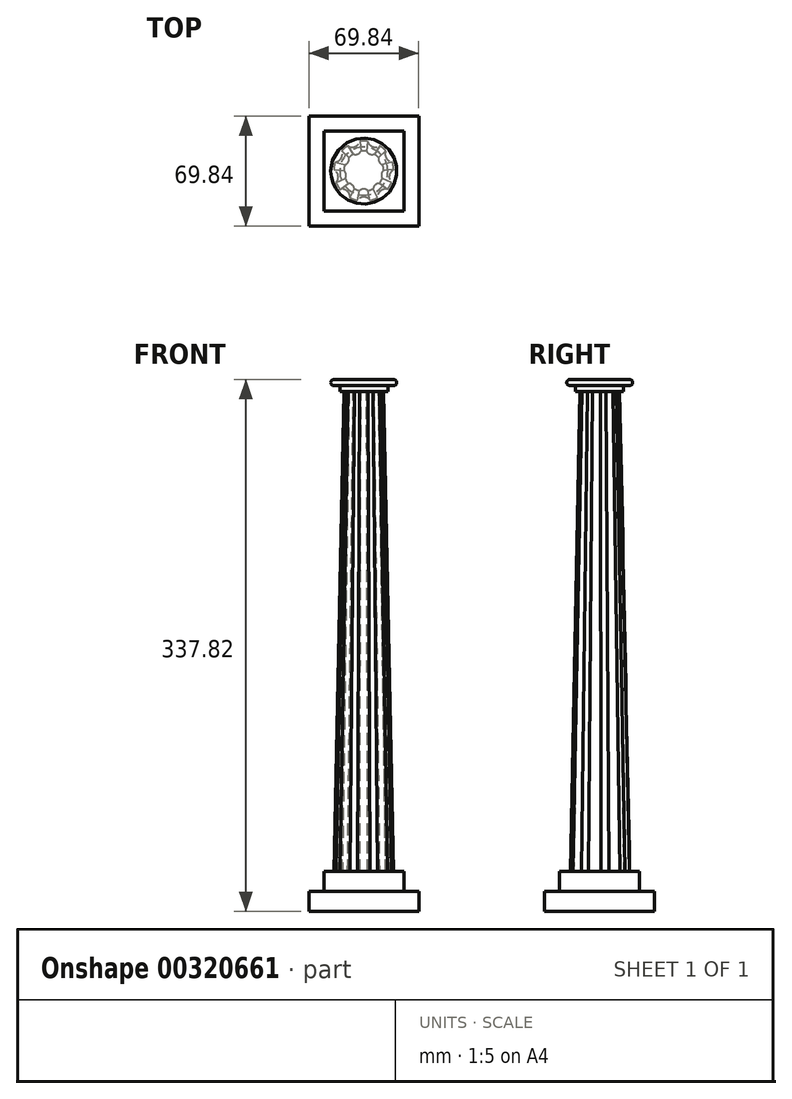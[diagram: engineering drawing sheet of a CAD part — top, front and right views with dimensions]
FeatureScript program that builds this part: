
annotation { "Feature Type Name" : "Feature", "Feature Type Description" : "" }
export const myFeature = defineFeature(function(context is Context, id is Id, definition is map)
    precondition{}
    {
        {
            var Q0;
            Q0=qCreatedBy(makeId("Top.planeOp"),FACE);
            var sketch = newSketch(context, id + "F0", { "sketchPlane" : qUnion([Q0])});
            skCircle(sketch, "E0", {"center": v(0, 0) * mm, "radius": 19.05 * mm});
            skArc(sketch, "E1", {"start": v(4.1, -18.6) * mm, "mid": v(0, -16.51) * mm, "end": v(-4.1, -18.6) * mm});
            skArc(sketch, "E2.1.0", {"start": v(15.1, -11.6) * mm, "mid": v(10.61, -12.65) * mm, "end": v(8.8, -16.9) * mm});
            skArc(sketch, "E2.2.0", {"start": v(19.03, 0.82) * mm, "mid": v(16.26, -2.87) * mm, "end": v(17.6, -7.28) * mm});
            skArc(sketch, "E2.3.0", {"start": v(14.06, 12.86) * mm, "mid": v(14.3, 8.25) * mm, "end": v(18.16, 5.74) * mm});
            skArc(sketch, "E2.4.0", {"start": v(2.5, 18.89) * mm, "mid": v(5.65, 15.51) * mm, "end": v(10.22, 16.07) * mm});
            skArc(sketch, "E2.5.0", {"start": v(-10.22, 16.07) * mm, "mid": v(-5.65, 15.51) * mm, "end": v(-2.5, 18.89) * mm});
            skArc(sketch, "E2.6.0", {"start": v(-18.16, 5.74) * mm, "mid": v(-14.3, 8.26) * mm, "end": v(-14.06, 12.86) * mm});
            skArc(sketch, "E2.7.0", {"start": v(-17.6, -7.28) * mm, "mid": v(-16.26, -2.87) * mm, "end": v(-19.03, 0.82) * mm});
            skArc(sketch, "E2.8.0", {"start": v(-8.8, -16.9) * mm, "mid": v(-10.61, -12.65) * mm, "end": v(-15.1, -11.6) * mm});
            skSolve(sketch);
        }
        {
            var Q0;
            Q0=qCreatedBy(makeId("Top.planeOp"),FACE);
            cPlane(context, id + "F1", {"entities" : qUnion([Q0]), "cplaneType" : CPlaneType.OFFSET, "offset" : 304.8 * mm, "width" : 152.4 * mm, "height" : 152.4 * mm});
        }
        {
            var Q0;
            Q0=qCreatedBy(id+"F1.planeOp",FACE);
            var sketch = newSketch(context, id + "F2", { "sketchPlane" : qUnion([Q0])});
            skCircle(sketch, "E3", {"center": v(0, 0) * mm, "radius": 12.7 * mm});
            skArc(sketch, "E4", {"start": v(2.58, -12.44) * mm, "mid": v(0, -11.43) * mm, "end": v(-2.58, -12.44) * mm});
            skArc(sketch, "E5.1.0", {"start": v(9.97, -7.87) * mm, "mid": v(7.35, -8.76) * mm, "end": v(6.02, -11.18) * mm});
            skArc(sketch, "E5.2.0", {"start": v(12.7, 0.38) * mm, "mid": v(11.26, -1.98) * mm, "end": v(11.8, -4.7) * mm});
            skArc(sketch, "E5.3.0", {"start": v(9.48, 8.45) * mm, "mid": v(9.9, 5.71) * mm, "end": v(12.06, 3.98) * mm});
            skArc(sketch, "E5.4.0", {"start": v(1.83, 12.57) * mm, "mid": v(3.9, 10.74) * mm, "end": v(6.68, 10.8) * mm});
            skArc(sketch, "E5.5.0", {"start": v(-6.68, 10.8) * mm, "mid": v(-3.9, 10.74) * mm, "end": v(-1.83, 12.57) * mm});
            skArc(sketch, "E5.6.0", {"start": v(-12.06, 3.98) * mm, "mid": v(-9.9, 5.72) * mm, "end": v(-9.48, 8.45) * mm});
            skArc(sketch, "E5.7.0", {"start": v(-11.8, -4.7) * mm, "mid": v(-11.26, -1.98) * mm, "end": v(-12.7, 0.38) * mm});
            skArc(sketch, "E5.8.0", {"start": v(-6.02, -11.18) * mm, "mid": v(-7.35, -8.76) * mm, "end": v(-9.97, -7.87) * mm});
            skSolve(sketch);
        }
        {
            var Q0;
            {var subQ0=sQuery(id+"F0.wireOp",EDGE,"E1");Q0=makeQuery(id+"F0.imprint","IMPRINT",FACE,{"disambiguationData":[TD([[makeQuery(id+"F0.imprint","IMPRINT",EDGE,{"derivedFrom":subQ0}),-1.0]])]});}
            var Q1;
            {var subQ0=sQuery(id+"F2.wireOp",EDGE,"E4");Q1=makeQuery(id+"F2.imprint","IMPRINT",FACE,{"disambiguationData":[TD([[makeQuery(id+"F2.imprint","IMPRINT",EDGE,{"derivedFrom":subQ0}),-1.0]])]});}
            loft(context, id + "F3", {"sheetProfilesArray" : [{ "sheetProfileEntities" : qUnion([Q0]) }, { "sheetProfileEntities" : qUnion([Q1]) }]});
        }
        {
            var Q0;
            Q0=qCreatedBy(makeId("Right.planeOp"),FACE);
            var sketch = newSketch(context, id + "F4", { "sketchPlane" : qUnion([Q0])});
            skLineSegment(sketch, "E6", {"start": v(0, 304.8) * mm, "end": v(0, 312.42) * mm});
            skLineSegment(sketch, "E7", {"start": v(0, 312.42) * mm, "end": v(19.05, 312.42) * mm});
            skLineSegment(sketch, "E8", {"start": v(0, 304.8) * mm, "end": v(15.24, 304.8) * mm});
            skLineSegment(sketch, "E9", {"start": v(15.24, 304.8) * mm, "end": v(15.24, 308.6) * mm});
            skLineSegment(sketch, "E10", {"start": v(15.24, 308.6) * mm, "end": v(19.05, 308.6) * mm});
            skLineSegment(sketch, "E11", {"start": v(19.05, 308.6) * mm, "end": v(19.05, 312.42) * mm});
            skCircle(sketch, "E12", {"center": v(19.05, 310.51) * mm, "radius": 1.9 * mm});
            skSolve(sketch);
        }
        {
            var Q0;
            Q0=makeQuery(id+"F4.imprint","IMPRINT",FACE,{"disambiguationData":[TD([[makeQuery(id+"F4.imprint","IMPRINT",EDGE,{"derivedFrom":sQuery(id+"F4.wireOp",EDGE,"E6")}),-1.0]])]});
            var Q1;
            {var subQ0=sQuery(id+"F4.wireOp",EDGE,"E11");Q1=makeQuery(id+"F4.imprint","IMPRINT",FACE,{"disambiguationData":[TD([[makeQuery(id+"F4.imprint","IMPRINT",EDGE,{"derivedFrom":subQ0}),1.0]])]});}
            var Q2;
            {var subQ0=sQuery(id+"F4.wireOp",EDGE,"E11");Q2=makeQuery(id+"F4.imprint","IMPRINT",FACE,{"disambiguationData":[TD([[makeQuery(id+"F4.imprint","IMPRINT",EDGE,{"derivedFrom":subQ0}),-1.0]])]});}
            var Q3;
            Q3=sQuery(id+"F4.wireOp",EDGE,"E6");
            revolve(context, id + "F5", {"operationType" : NewBodyOperationType.ADD, "entities" : qUnion([Q0, Q1, Q2]), "axis" : qUnion([Q3]), "revolveType" : RevolveType.FULL});
        }
        {
            var Q0;
            Q0=qCreatedBy(makeId("Top.planeOp"),FACE);
            var sketch = newSketch(context, id + "F6", { "sketchPlane" : qUnion([Q0])});
            skLineSegment(sketch, "E13.bottom", {"start": v(25.4, 25.4) * mm, "end": v(-25.4, 25.4) * mm});
            skLineSegment(sketch, "E13.top", {"start": v(25.4, -25.4) * mm, "end": v(-25.4, -25.4) * mm});
            skLineSegment(sketch, "E13.left", {"start": v(25.4, 25.4) * mm, "end": v(25.4, -25.4) * mm});
            skLineSegment(sketch, "E13.right", {"start": v(-25.4, 25.4) * mm, "end": v(-25.4, -25.4) * mm});
            skPoint(sketch, "E13.middle", {"position": v(0, 0) * mm});
            skSolve(sketch);
        }
        {
            var Q0;
            Q0=makeQuery(id+"F6.imprint","IMPRINT",FACE,{"disambiguationData":[TD([[makeQuery(id+"F6.imprint","IMPRINT",EDGE,{"derivedFrom":sQuery(id+"F6.wireOp",EDGE,"E13.bottom")}),1.0]])]});
            extrude(context, id + "F7", {"entities" : qUnion([Q0]), "operationType" : NewBodyOperationType.ADD, "oppositeDirection" : true, "depth" : 12.7 * mm});
        }
        {
            var Q0;
            Q0=makeQuery(id+"F7.opExtrude","CAP_FACE",FACE,{"disambiguationData":[OSD([sQuery(id+"F6.wireOp",EDGE,"E13.bottom"),sQuery(id+"F6.wireOp",EDGE,"E13.top"),sQuery(id+"F6.wireOp",EDGE,"E13.left"),sQuery(id+"F6.wireOp",EDGE,"E13.right")])],"isStart":false});
            var sketch = newSketch(context, id + "F8", { "sketchPlane" : qUnion([Q0])});
            skLineSegment(sketch, "E14.bottom", {"start": v(34.93, -34.92) * mm, "end": v(-34.92, -34.93) * mm});
            skLineSegment(sketch, "E14.top", {"start": v(34.92, 34.93) * mm, "end": v(-34.93, 34.92) * mm});
            skLineSegment(sketch, "E14.left", {"start": v(34.93, -34.92) * mm, "end": v(34.93, 34.93) * mm});
            skLineSegment(sketch, "E14.right", {"start": v(-34.92, -34.92) * mm, "end": v(-34.93, 34.92) * mm});
            skPoint(sketch, "E14.middle", {"position": v(0, 0) * mm});
            skSolve(sketch);
        }
        {
            var Q0;
            Q0=makeQuery(id+"F8.imprint","IMPRINT",FACE,{"disambiguationData":[TD([[makeQuery(id+"F8.imprint","IMPRINT",EDGE,{"derivedFrom":sQuery(id+"F8.wireOp",EDGE,"E14.bottom")}),-1.0]])]});
            var Q1;
            Q1=makeQuery(id+"F8.imprint","IMPRINT",FACE,{"disambiguationData":[TD([[makeQuery(id+"F8.imprint","IMPRINT",EDGE,{"derivedFrom":makeQuery(id+"F7.opExtrude","CAP_EDGE",EDGE,{"disambiguationData":[OSD([sQuery(id+"F6.wireOp",EDGE,"E13.bottom")])],"isStart":false})}),-1.0]])]});
            extrude(context, id + "F9", {"entities" : qUnion([Q0, Q1]), "operationType" : NewBodyOperationType.ADD, "depth" : 12.7 * mm});
        }
    });
